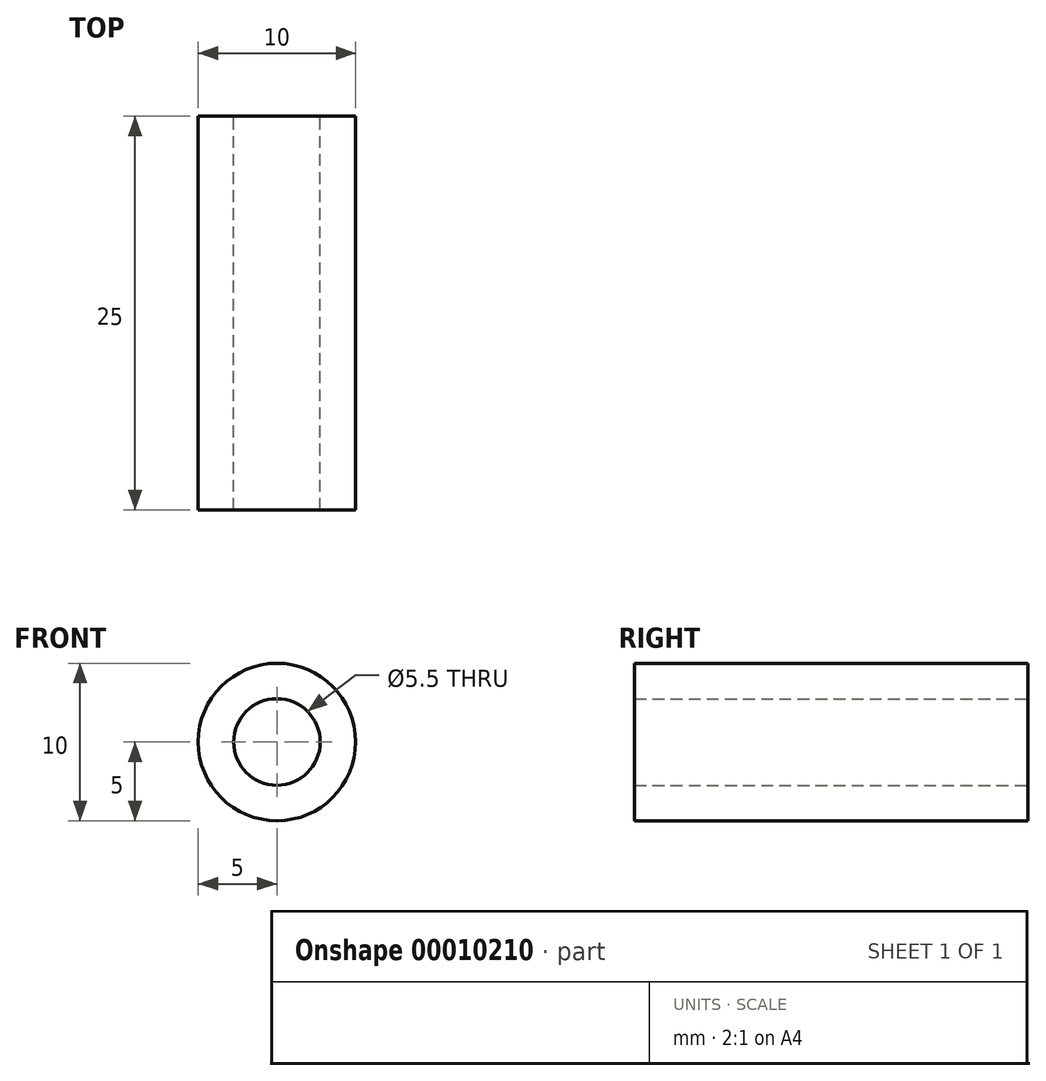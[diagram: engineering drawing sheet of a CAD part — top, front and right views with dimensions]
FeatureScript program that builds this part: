
annotation { "Feature Type Name" : "Feature", "Feature Type Description" : "" }
export const myFeature = defineFeature(function(context is Context, id is Id, definition is map)
    precondition{}
    {
        {
            var Q0;
            Q0=qCreatedBy(makeId("Front.planeOp"),FACE);
            var sketch = newSketch(context, id + "F0", { "sketchPlane" : qUnion([Q0])});
            skCircle(sketch, "E0", {"center": v(0, 0) * mm, "radius": 2.75 * mm});
            skCircle(sketch, "E1", {"center": v(0, 0) * mm, "radius": 5 * mm});
            skSolve(sketch);
        }
        {
            var Q0;
            Q0 = qSketchRegion(id + "F0", true);
            extrude(context, id + "F1", {"entities" : qUnion([Q0]), "depth" : 25 * mm});
        }
    });
